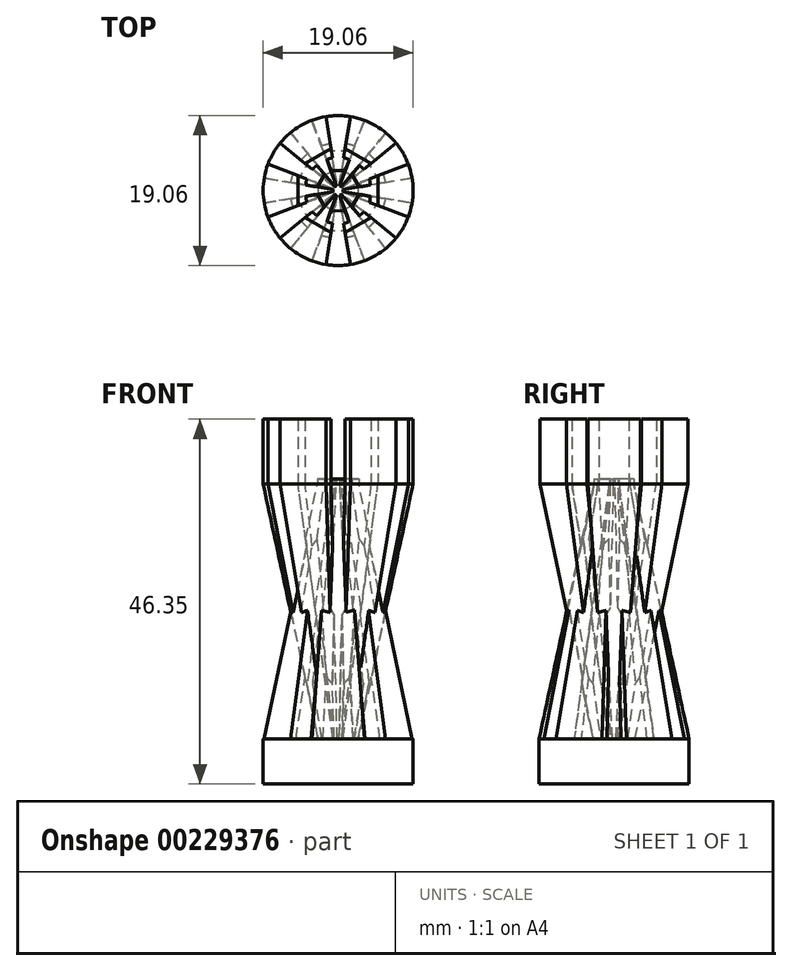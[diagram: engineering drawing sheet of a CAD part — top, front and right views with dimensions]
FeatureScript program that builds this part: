
annotation { "Feature Type Name" : "Feature", "Feature Type Description" : "" }
export const myFeature = defineFeature(function(context is Context, id is Id, definition is map)
    precondition{}
    {
        {
            var Q0;
            Q0=qCreatedBy(makeId("Top.planeOp"),FACE);
            var sketch = newSketch(context, id + "F0", { "sketchPlane" : qUnion([Q0])});
            skCircle(sketch, "E0", {"center": v(0, 0) * mm, "radius": 9.53 * mm});
            skSolve(sketch);
        }
        {
            var Q0;
            Q0=makeQuery(id+"F0.imprint","IMPRINT",FACE,{"disambiguationData":[TD([[makeQuery(id+"F0.imprint","IMPRINT",EDGE,{"derivedFrom":sQuery(id+"F0.wireOp",EDGE,"E0")}),1.0]])]});
            extrude(context, id + "F1", {"entities" : qUnion([Q0]), "depth" : 5.7 * mm});
        }
        {
            var Q0;
            Q0=qCreatedBy(makeId("Top.planeOp"),FACE);
            cPlane(context, id + "F2", {"entities" : qUnion([Q0]), "cplaneType" : CPlaneType.OFFSET, "offset" : 38.1 * mm, "width" : 152.4 * mm, "height" : 152.4 * mm});
        }
        {
            var Q0;
            Q0=makeQuery(id+"F1.opExtrude","CAP_FACE",FACE,{"disambiguationData":[OSD([sQuery(id+"F0.wireOp",EDGE,"E0")])],"isStart":false});
            var sketch = newSketch(context, id + "F3", { "sketchPlane" : qUnion([Q0])});
            skCircle(sketch, "E1", {"center": v(0, 0) * mm, "radius": 0.64 * mm});
            skCircle(sketch, "E2", {"center": v(0, 0) * mm, "radius": 9.53 * mm});
            skLineSegment(sketch, "E3", {"start": v(-1.9, -5.08) * mm, "end": v(-3.34, -8.92) * mm});
            skLineSegment(sketch, "E4", {"start": v(1.9, -5.08) * mm, "end": v(3.34, -8.92) * mm});
            skLineSegment(sketch, "E5.1.2", {"start": v(5.35, -0.9) * mm, "end": v(9.4, -1.56) * mm});
            skLineSegment(sketch, "E5.1.3", {"start": v(3.45, -4.19) * mm, "end": v(6.05, -7.36) * mm});
            skLineSegment(sketch, "E5.2.2", {"start": v(3.45, 4.19) * mm, "end": v(6.05, 7.36) * mm});
            skLineSegment(sketch, "E5.2.3", {"start": v(5.35, 0.9) * mm, "end": v(9.4, 1.56) * mm});
            skLineSegment(sketch, "E6.6.3.0", {"start": v(-1.9, 5.08) * mm, "end": v(-3.34, 8.92) * mm});
            skLineSegment(sketch, "E6.9.3.0", {"start": v(1.9, 5.08) * mm, "end": v(3.34, 8.92) * mm});
            skLineSegment(sketch, "E6.6.4.0", {"start": v(-5.35, 0.9) * mm, "end": v(-9.4, 1.56) * mm});
            skLineSegment(sketch, "E6.9.4.0", {"start": v(-3.45, 4.19) * mm, "end": v(-6.05, 7.36) * mm});
            skLineSegment(sketch, "E6.6.5.0", {"start": v(-3.45, -4.19) * mm, "end": v(-6.05, -7.36) * mm});
            skLineSegment(sketch, "E6.9.5.0", {"start": v(-5.35, -0.9) * mm, "end": v(-9.4, -1.56) * mm});
            skLineSegment(sketch, "E7", {"start": v(0, 0) * mm, "end": v(0, 2.28) * mm});
            skLineSegment(sketch, "E8", {"start": v(0.5, 2.64) * mm, "end": v(0.12, 0.62) * mm});
            skLineSegment(sketch, "E9", {"start": v(2.04, 1.76) * mm, "end": v(0.48, 0.41) * mm});
            skLineSegment(sketch, "E10.1.0", {"start": v(-2.04, 1.76) * mm, "end": v(-0.48, 0.41) * mm});
            skLineSegment(sketch, "E10.1.3", {"start": v(-0.5, 2.64) * mm, "end": v(-0.12, 0.62) * mm});
            skLineSegment(sketch, "E10.2.0", {"start": v(-2.54, -0.89) * mm, "end": v(-0.6, -0.2) * mm});
            skLineSegment(sketch, "E10.2.3", {"start": v(-2.54, 0.89) * mm, "end": v(-0.6, 0.2) * mm});
            skLineSegment(sketch, "E10.3.0", {"start": v(-0.5, -2.64) * mm, "end": v(-0.12, -0.62) * mm});
            skLineSegment(sketch, "E10.3.3", {"start": v(-2.04, -1.76) * mm, "end": v(-0.48, -0.41) * mm});
            skLineSegment(sketch, "E10.4.0", {"start": v(2.04, -1.76) * mm, "end": v(0.48, -0.41) * mm});
            skLineSegment(sketch, "E10.4.3", {"start": v(0.5, -2.64) * mm, "end": v(0.12, -0.62) * mm});
            skLineSegment(sketch, "E10.5.0", {"start": v(2.54, 0.89) * mm, "end": v(0.6, 0.2) * mm});
            skLineSegment(sketch, "E10.5.3", {"start": v(2.54, -0.89) * mm, "end": v(0.6, -0.2) * mm});
            skLineSegment(sketch, "E11", {"start": v(-2.54, 0.89) * mm, "end": v(-2.54, -0.89) * mm});
            skLineSegment(sketch, "E12", {"start": v(-2.04, 1.76) * mm, "end": v(-0.5, 2.64) * mm});
            skLineSegment(sketch, "E13", {"start": v(0.5, 2.64) * mm, "end": v(2.04, 1.76) * mm});
            skLineSegment(sketch, "E14", {"start": v(2.54, 0.89) * mm, "end": v(2.54, -0.89) * mm});
            skLineSegment(sketch, "E15", {"start": v(2.04, -1.76) * mm, "end": v(0.5, -2.64) * mm});
            skLineSegment(sketch, "E16", {"start": v(-0.5, -2.64) * mm, "end": v(-2.04, -1.76) * mm});
            skLineSegment(sketch, "E17", {"start": v(-5.35, -0.9) * mm, "end": v(-3.45, -4.19) * mm});
            skLineSegment(sketch, "E18", {"start": v(-1.9, -5.08) * mm, "end": v(1.9, -5.08) * mm});
            skLineSegment(sketch, "E19", {"start": v(3.45, -4.19) * mm, "end": v(5.35, -0.9) * mm});
            skLineSegment(sketch, "E20", {"start": v(3.45, 4.19) * mm, "end": v(5.35, 0.9) * mm});
            skLineSegment(sketch, "E21", {"start": v(-1.9, 5.08) * mm, "end": v(1.9, 5.08) * mm});
            skLineSegment(sketch, "E22", {"start": v(-3.45, 4.19) * mm, "end": v(-5.35, 0.9) * mm});
            skSolve(sketch);
        }
        {
            var Q0;
            Q0=qCreatedBy(id+"F2.planeOp",FACE);
            var sketch = newSketch(context, id + "F4", { "sketchPlane" : qUnion([Q0])});
            skArc(sketch, "E23", {"start": v(1.56, -9.4) * mm, "mid": v(4.76, -8.25) * mm, "end": v(7.36, -6.05) * mm});
            skLineSegment(sketch, "E24", {"start": v(-4.19, 3.45) * mm, "end": v(-7.36, 6.05) * mm});
            skLineSegment(sketch, "E25", {"start": v(-0.9, 5.35) * mm, "end": v(-1.56, 9.4) * mm});
            skLineSegment(sketch, "E26.1.2", {"start": v(-5.08, 1.9) * mm, "end": v(-8.92, 3.34) * mm});
            skLineSegment(sketch, "E26.1.3", {"start": v(-5.08, -1.9) * mm, "end": v(-8.92, -3.34) * mm});
            skLineSegment(sketch, "E26.2.2", {"start": v(-4.19, -3.45) * mm, "end": v(-7.36, -6.05) * mm});
            skLineSegment(sketch, "E26.2.3", {"start": v(-0.9, -5.35) * mm, "end": v(-1.56, -9.4) * mm});
            skLineSegment(sketch, "E26.3.2", {"start": v(0.9, -5.35) * mm, "end": v(1.56, -9.4) * mm});
            skLineSegment(sketch, "E26.3.3", {"start": v(4.19, -3.45) * mm, "end": v(7.36, -6.05) * mm});
            skLineSegment(sketch, "E26.4.2", {"start": v(5.08, -1.9) * mm, "end": v(8.92, -3.34) * mm});
            skLineSegment(sketch, "E26.4.3", {"start": v(5.08, 1.9) * mm, "end": v(8.92, 3.34) * mm});
            skLineSegment(sketch, "E26.5.2", {"start": v(4.19, 3.45) * mm, "end": v(7.36, 6.05) * mm});
            skLineSegment(sketch, "E26.5.3", {"start": v(0.9, 5.35) * mm, "end": v(1.56, 9.4) * mm});
            skCircle(sketch, "E27", {"center": v(0, 0) * mm, "radius": 0.64 * mm});
            skLineSegment(sketch, "E28", {"start": v(-0.89, -2.54) * mm, "end": v(-0.2, -0.6) * mm});
            skLineSegment(sketch, "E29", {"start": v(0.89, -2.6) * mm, "end": v(0.2, -0.6) * mm});
            skLineSegment(sketch, "E30.1.0", {"start": v(2.64, -0.5) * mm, "end": v(0.62, -0.12) * mm});
            skLineSegment(sketch, "E30.1.3", {"start": v(1.76, -2.04) * mm, "end": v(0.41, -0.48) * mm});
            skLineSegment(sketch, "E30.2.0", {"start": v(1.76, 2.04) * mm, "end": v(0.41, 0.48) * mm});
            skLineSegment(sketch, "E30.2.3", {"start": v(2.64, 0.5) * mm, "end": v(0.62, 0.12) * mm});
            skLineSegment(sketch, "E30.3.0", {"start": v(-0.89, 2.54) * mm, "end": v(-0.2, 0.6) * mm});
            skLineSegment(sketch, "E30.3.3", {"start": v(0.89, 2.54) * mm, "end": v(0.2, 0.6) * mm});
            skLineSegment(sketch, "E30.4.0", {"start": v(-2.64, 0.5) * mm, "end": v(-0.62, 0.12) * mm});
            skLineSegment(sketch, "E30.4.3", {"start": v(-1.76, 2.04) * mm, "end": v(-0.41, 0.48) * mm});
            skLineSegment(sketch, "E30.5.0", {"start": v(-1.76, -2.04) * mm, "end": v(-0.41, -0.48) * mm});
            skLineSegment(sketch, "E30.5.3", {"start": v(-2.64, -0.5) * mm, "end": v(-0.62, -0.12) * mm});
            skLineSegment(sketch, "E31", {"start": v(-4.19, -3.45) * mm, "end": v(-0.9, -5.35) * mm});
            skLineSegment(sketch, "E32", {"start": v(-4.19, 3.45) * mm, "end": v(-0.9, 5.35) * mm});
            skLineSegment(sketch, "E33", {"start": v(0.9, 5.35) * mm, "end": v(4.19, 3.45) * mm});
            skLineSegment(sketch, "E34", {"start": v(5.08, 1.9) * mm, "end": v(5.08, -1.9) * mm});
            skLineSegment(sketch, "E35", {"start": v(4.19, -3.45) * mm, "end": v(0.9, -5.35) * mm});
            skLineSegment(sketch, "E36", {"start": v(-5.08, -1.9) * mm, "end": v(-5.08, 1.9) * mm});
            skLineSegment(sketch, "E37", {"start": v(-0.89, 2.54) * mm, "end": v(0.89, 2.54) * mm});
            skLineSegment(sketch, "E38", {"start": v(-1.76, 2.04) * mm, "end": v(-2.64, 0.5) * mm});
            skLineSegment(sketch, "E39", {"start": v(-2.64, -0.5) * mm, "end": v(-1.76, -2.04) * mm});
            skLineSegment(sketch, "E40", {"start": v(-0.89, -2.54) * mm, "end": v(0.89, -2.6) * mm});
            skLineSegment(sketch, "E41", {"start": v(1.76, 2.04) * mm, "end": v(2.64, 0.5) * mm});
            skLineSegment(sketch, "E42", {"start": v(2.64, -0.5) * mm, "end": v(1.76, -2.04) * mm});
            skArc(sketch, "E43.trimOffspring", {"start": v(-7.36, -6.05) * mm, "mid": v(-4.76, -8.25) * mm, "end": v(-1.56, -9.4) * mm});
            skArc(sketch, "E44.trimOffspring", {"start": v(8.92, -3.34) * mm, "mid": v(9.53, 0) * mm, "end": v(8.92, 3.34) * mm});
            skArc(sketch, "E45.trimOffspring", {"start": v(7.36, 6.05) * mm, "mid": v(4.76, 8.25) * mm, "end": v(1.56, 9.4) * mm});
            skArc(sketch, "E46.trimOffspring", {"start": v(-1.56, 9.4) * mm, "mid": v(-4.76, 8.25) * mm, "end": v(-7.36, 6.05) * mm});
            skArc(sketch, "E47.trimOffspring", {"start": v(-8.92, 3.34) * mm, "mid": v(-9.53, 0) * mm, "end": v(-8.92, -3.34) * mm});
            skSolve(sketch);
        }
        {
            var Q1;
            {var subQ1=sQuery(id+"F3.wireOp",EDGE,"E10.3.0");Q1=makeQuery(id+"F3.imprint","IMPRINT",FACE,{"disambiguationData":[TD([[makeQuery(id+"F3.imprint","IMPRINT",EDGE,{"derivedFrom":subQ1}),1.0]])]});}
            var Q2;
            {var subQ1=sQuery(id+"F4.wireOp",EDGE,"E26.2.2");Q2=makeQuery(id+"F4.imprint","IMPRINT",FACE,{"disambiguationData":[TD([[makeQuery(id+"F4.imprint","IMPRINT",EDGE,{"derivedFrom":subQ1}),1.0]])]});}
            loft(context, id + "F5", {"operationType" : NewBodyOperationType.ADD, "sheetProfilesArray" : [{ "sheetProfileEntities" : qUnion([Q1]) }, { "sheetProfileEntities" : qUnion([Q2]) }]});
        }
        {
            var Q1;
            {var subQ1=sQuery(id+"F4.wireOp",EDGE,"E26.3.2");Q1=makeQuery(id+"F4.imprint","IMPRINT",FACE,{"disambiguationData":[TD([[makeQuery(id+"F4.imprint","IMPRINT",EDGE,{"derivedFrom":subQ1}),1.0]])]});}
            var Q2;
            {var subQ1=sQuery(id+"F3.wireOp",EDGE,"E10.4.0");Q2=makeQuery(id+"F3.imprint","IMPRINT",FACE,{"disambiguationData":[TD([[makeQuery(id+"F3.imprint","IMPRINT",EDGE,{"derivedFrom":subQ1}),1.0]])]});}
            loft(context, id + "F6", {"operationType" : NewBodyOperationType.ADD, "sheetProfilesArray" : [{ "sheetProfileEntities" : qUnion([Q1]) }, { "sheetProfileEntities" : qUnion([Q2]) }]});
        }
        {
            var Q1;
            {var subQ1=sQuery(id+"F3.wireOp",EDGE,"E10.5.0");Q1=makeQuery(id+"F3.imprint","IMPRINT",FACE,{"disambiguationData":[TD([[makeQuery(id+"F3.imprint","IMPRINT",EDGE,{"derivedFrom":subQ1}),1.0]])]});}
            var Q2;
            {var subQ1=sQuery(id+"F4.wireOp",EDGE,"E26.4.2");Q2=makeQuery(id+"F4.imprint","IMPRINT",FACE,{"disambiguationData":[TD([[makeQuery(id+"F4.imprint","IMPRINT",EDGE,{"derivedFrom":subQ1}),1.0]])]});}
            loft(context, id + "F7", {"operationType" : NewBodyOperationType.ADD, "sheetProfilesArray" : [{ "sheetProfileEntities" : qUnion([Q1]) }, { "sheetProfileEntities" : qUnion([Q2]) }]});
        }
        {
            var Q1;
            {var subQ1=sQuery(id+"F3.wireOp",EDGE,"E8");Q1=makeQuery(id+"F3.imprint","IMPRINT",FACE,{"disambiguationData":[TD([[makeQuery(id+"F3.imprint","IMPRINT",EDGE,{"derivedFrom":subQ1}),1.0]])]});}
            var Q2;
            {var subQ1=sQuery(id+"F4.wireOp",EDGE,"E26.5.2");Q2=makeQuery(id+"F4.imprint","IMPRINT",FACE,{"disambiguationData":[TD([[makeQuery(id+"F4.imprint","IMPRINT",EDGE,{"derivedFrom":subQ1}),1.0]])]});}
            loft(context, id + "F8", {"operationType" : NewBodyOperationType.ADD, "sheetProfilesArray" : [{ "sheetProfileEntities" : qUnion([Q1]) }, { "sheetProfileEntities" : qUnion([Q2]) }]});
        }
        {
            var Q1;
            {var subQ1=sQuery(id+"F3.wireOp",EDGE,"E10.1.0");Q1=makeQuery(id+"F3.imprint","IMPRINT",FACE,{"disambiguationData":[TD([[makeQuery(id+"F3.imprint","IMPRINT",EDGE,{"derivedFrom":subQ1}),1.0]])]});}
            var Q2;
            {var subQ1=sQuery(id+"F4.wireOp",EDGE,"E24");Q2=makeQuery(id+"F4.imprint","IMPRINT",FACE,{"disambiguationData":[TD([[makeQuery(id+"F4.imprint","IMPRINT",EDGE,{"derivedFrom":subQ1}),-1.0]])]});}
            loft(context, id + "F9", {"operationType" : NewBodyOperationType.ADD, "sheetProfilesArray" : [{ "sheetProfileEntities" : qUnion([Q1]) }, { "sheetProfileEntities" : qUnion([Q2]) }]});
        }
        {
            var Q1;
            {var subQ1=sQuery(id+"F3.wireOp",EDGE,"E10.2.0");Q1=makeQuery(id+"F3.imprint","IMPRINT",FACE,{"disambiguationData":[TD([[makeQuery(id+"F3.imprint","IMPRINT",EDGE,{"derivedFrom":subQ1}),1.0]])]});}
            var Q2;
            {var subQ1=sQuery(id+"F4.wireOp",EDGE,"E26.1.2");Q2=makeQuery(id+"F4.imprint","IMPRINT",FACE,{"disambiguationData":[TD([[makeQuery(id+"F4.imprint","IMPRINT",EDGE,{"derivedFrom":subQ1}),1.0]])]});}
            loft(context, id + "F10", {"operationType" : NewBodyOperationType.ADD, "sheetProfilesArray" : [{ "sheetProfileEntities" : qUnion([Q1]) }, { "sheetProfileEntities" : qUnion([Q2]) }]});
        }
        {
            var Q1;
            {var subQ1=sQuery(id+"F3.wireOp",EDGE,"E6.6.4.0");Q1=makeQuery(id+"F3.imprint","IMPRINT",FACE,{"disambiguationData":[TD([[makeQuery(id+"F3.imprint","IMPRINT",EDGE,{"derivedFrom":subQ1}),-1.0]])]});}
            var Q2;
            {var subQ1=sQuery(id+"F4.wireOp",EDGE,"E30.4.0");Q2=makeQuery(id+"F4.imprint","IMPRINT",FACE,{"disambiguationData":[TD([[makeQuery(id+"F4.imprint","IMPRINT",EDGE,{"derivedFrom":subQ1}),1.0]])]});}
            loft(context, id + "F11", {"operationType" : NewBodyOperationType.ADD, "sheetProfilesArray" : [{ "sheetProfileEntities" : qUnion([Q1]) }, { "sheetProfileEntities" : qUnion([Q2]) }]});
        }
        {
            var Q1;
            {var subQ1=sQuery(id+"F3.wireOp",EDGE,"E6.6.3.0");Q1=makeQuery(id+"F3.imprint","IMPRINT",FACE,{"disambiguationData":[TD([[makeQuery(id+"F3.imprint","IMPRINT",EDGE,{"derivedFrom":subQ1}),-1.0]])]});}
            var Q2;
            {var subQ1=sQuery(id+"F4.wireOp",EDGE,"E30.3.0");Q2=makeQuery(id+"F4.imprint","IMPRINT",FACE,{"disambiguationData":[TD([[makeQuery(id+"F4.imprint","IMPRINT",EDGE,{"derivedFrom":subQ1}),1.0]])]});}
            loft(context, id + "F12", {"operationType" : NewBodyOperationType.ADD, "sheetProfilesArray" : [{ "sheetProfileEntities" : qUnion([Q1]) }, { "sheetProfileEntities" : qUnion([Q2]) }]});
        }
        {
            var Q1;
            {var subQ1=sQuery(id+"F3.wireOp",EDGE,"E5.2.2");Q1=makeQuery(id+"F3.imprint","IMPRINT",FACE,{"disambiguationData":[TD([[makeQuery(id+"F3.imprint","IMPRINT",EDGE,{"derivedFrom":subQ1}),-1.0]])]});}
            var Q2;
            {var subQ1=sQuery(id+"F4.wireOp",EDGE,"E30.2.0");Q2=makeQuery(id+"F4.imprint","IMPRINT",FACE,{"disambiguationData":[TD([[makeQuery(id+"F4.imprint","IMPRINT",EDGE,{"derivedFrom":subQ1}),1.0]])]});}
            loft(context, id + "F13", {"operationType" : NewBodyOperationType.ADD, "sheetProfilesArray" : [{ "sheetProfileEntities" : qUnion([Q1]) }, { "sheetProfileEntities" : qUnion([Q2]) }]});
        }
        {
            var Q1;
            {var subQ1=sQuery(id+"F4.wireOp",EDGE,"E30.5.0");Q1=makeQuery(id+"F4.imprint","IMPRINT",FACE,{"disambiguationData":[TD([[makeQuery(id+"F4.imprint","IMPRINT",EDGE,{"derivedFrom":subQ1}),1.0]])]});}
            var Q2;
            {var subQ1=sQuery(id+"F3.wireOp",EDGE,"E6.6.5.0");Q2=makeQuery(id+"F3.imprint","IMPRINT",FACE,{"disambiguationData":[TD([[makeQuery(id+"F3.imprint","IMPRINT",EDGE,{"derivedFrom":subQ1}),-1.0]])]});}
            loft(context, id + "F14", {"operationType" : NewBodyOperationType.ADD, "sheetProfilesArray" : [{ "sheetProfileEntities" : qUnion([Q1]) }, { "sheetProfileEntities" : qUnion([Q2]) }]});
        }
        {
            var Q1;
            {var subQ1=sQuery(id+"F3.wireOp",EDGE,"E5.1.2");Q1=makeQuery(id+"F3.imprint","IMPRINT",FACE,{"disambiguationData":[TD([[makeQuery(id+"F3.imprint","IMPRINT",EDGE,{"derivedFrom":subQ1}),-1.0]])]});}
            var Q2;
            {var subQ1=sQuery(id+"F4.wireOp",EDGE,"E30.1.0");Q2=makeQuery(id+"F4.imprint","IMPRINT",FACE,{"disambiguationData":[TD([[makeQuery(id+"F4.imprint","IMPRINT",EDGE,{"derivedFrom":subQ1}),1.0]])]});}
            loft(context, id + "F15", {"operationType" : NewBodyOperationType.ADD, "sheetProfilesArray" : [{ "sheetProfileEntities" : qUnion([Q1]) }, { "sheetProfileEntities" : qUnion([Q2]) }]});
        }
        {
            var Q1;
            {var subQ1=sQuery(id+"F4.wireOp",EDGE,"E28");Q1=makeQuery(id+"F4.imprint","IMPRINT",FACE,{"disambiguationData":[TD([[makeQuery(id+"F4.imprint","IMPRINT",EDGE,{"derivedFrom":subQ1}),-1.0]])]});}
            var Q2;
            {var subQ1=sQuery(id+"F3.wireOp",EDGE,"E3");Q2=makeQuery(id+"F3.imprint","IMPRINT",FACE,{"disambiguationData":[TD([[makeQuery(id+"F3.imprint","IMPRINT",EDGE,{"derivedFrom":subQ1}),1.0]])]});}
            loft(context, id + "F16", {"operationType" : NewBodyOperationType.ADD, "sheetProfilesArray" : [{ "sheetProfileEntities" : qUnion([Q1]) }, { "sheetProfileEntities" : qUnion([Q2]) }]});
        }
        {
            var Q0;
            Q0=qSketchRegion(id+"F4",true);
            extrude(context, id + "F17", {"entities" : qUnion([Q0]), "operationType" : NewBodyOperationType.ADD, "depth" : 0.64 * mm});
        }
        {
            var Q0;
            Q0=makeQuery(id+"F17.opExtrude","CAP_FACE",FACE,{"disambiguationData":[OSD([sQuery(id+"F4.wireOp",EDGE,"E26.2.2"),sQuery(id+"F4.wireOp",EDGE,"E26.2.3"),sQuery(id+"F4.wireOp",EDGE,"E31"),sQuery(id+"F4.wireOp",EDGE,"E43.trimOffspring")])],"isStart":false});
            var Q1;
            Q1=makeQuery(id+"F17.opExtrude","CAP_FACE",FACE,{"disambiguationData":[OSD([sQuery(id+"F4.wireOp",EDGE,"E26.1.2"),sQuery(id+"F4.wireOp",EDGE,"E26.1.3"),sQuery(id+"F4.wireOp",EDGE,"E36"),sQuery(id+"F4.wireOp",EDGE,"E47.trimOffspring")])],"isStart":false});
            var Q2;
            Q2=makeQuery(id+"F17.opExtrude","CAP_FACE",FACE,{"disambiguationData":[OSD([sQuery(id+"F4.wireOp",EDGE,"E24"),sQuery(id+"F4.wireOp",EDGE,"E25"),sQuery(id+"F4.wireOp",EDGE,"E32"),sQuery(id+"F4.wireOp",EDGE,"E46.trimOffspring")])],"isStart":false});
            var Q3;
            Q3=makeQuery(id+"F17.opExtrude","CAP_FACE",FACE,{"disambiguationData":[OSD([sQuery(id+"F4.wireOp",EDGE,"E26.5.2"),sQuery(id+"F4.wireOp",EDGE,"E26.5.3"),sQuery(id+"F4.wireOp",EDGE,"E33"),sQuery(id+"F4.wireOp",EDGE,"E45.trimOffspring")])],"isStart":false});
            var Q4;
            Q4=makeQuery(id+"F17.opExtrude","CAP_FACE",FACE,{"disambiguationData":[OSD([sQuery(id+"F4.wireOp",EDGE,"E26.4.2"),sQuery(id+"F4.wireOp",EDGE,"E26.4.3"),sQuery(id+"F4.wireOp",EDGE,"E34"),sQuery(id+"F4.wireOp",EDGE,"E44.trimOffspring")])],"isStart":false});
            var Q5;
            Q5=makeQuery(id+"F17.opExtrude","CAP_FACE",FACE,{"disambiguationData":[OSD([sQuery(id+"F4.wireOp",EDGE,"E23"),sQuery(id+"F4.wireOp",EDGE,"E26.3.2"),sQuery(id+"F4.wireOp",EDGE,"E26.3.3"),sQuery(id+"F4.wireOp",EDGE,"E35")])],"isStart":false});
            extrude(context, id + "F18", {"entities" : qUnion([Q0, Q1, Q2, Q3, Q4, Q5]), "operationType" : NewBodyOperationType.ADD, "depth" : 7.62 * mm});
        }
    });
